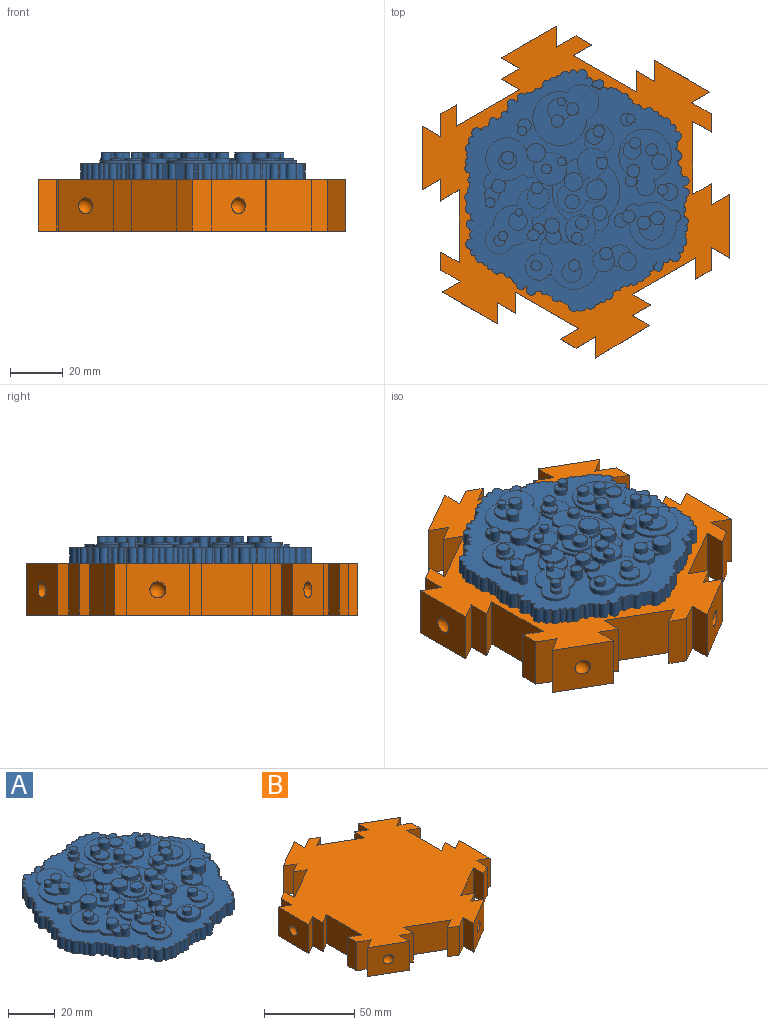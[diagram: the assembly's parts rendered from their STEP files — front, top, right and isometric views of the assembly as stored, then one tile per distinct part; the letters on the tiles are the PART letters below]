
ASSEMBLY  parts=2 mates=1
PART A: 301 faces, bbox 91.9x85.7x10 mm
  f0: cylinder r=4.09mm len=2.46mm, axis (0,0,-1), area 2.6mm2, adj f8,f185,f204,f299
  f1: cylinder r=4.09mm len=6.79mm, axis (0,0,-1), area 9.3mm2, adj f185,f204,f287,f299
  f2: cylinder r=2.88mm len=5.75mm, axis (0,0,-1), area 19.8mm2, adj f40,f41,f185,f191,f230,f297
  f3: cylinder r=2.79mm len=4.94mm, axis (0,0,-1), area 10.2mm2, adj f42,f185,f194,f227,f261,f295
  f4: cylinder r=2.79mm len=3.54mm, axis (0,0,-1), area 7.8mm2, adj f185,f227,f261,f295
  f5: cylinder r=2.49mm len=4.99mm, axis (0,0,-1), area 24.2mm2, adj f185,f225,f293
  f6: cylinder r=2.42mm len=4.85mm, axis (0,0,-1), area 23.1mm2, adj f185,f226,f291
  f7: cylinder r=3.19mm len=6.37mm, axis (0,0,-1), area 31.5mm2, adj f185,f229,f289
  f8: cylinder r=4.04mm len=8.09mm, axis (0,0,-1), area 30.1mm2, adj f0,f49,f50,f185,f191,f204,f216,f287
  f9: cylinder r=4.59mm len=8.54mm, axis (0,0,-1), area 16.5mm2, adj f203,f214,f283,f285
  f10: cylinder r=4.59mm len=1.25mm, axis (0,0,-1), area 1.7mm2, adj f203,f214,f283,f285
  f11: cylinder r=3.09mm len=4.48mm, axis (0,0,-1), area 6.8mm2, adj f185,f202,f203,f281
  f12: cylinder r=8.87mm len=16.72mm, axis (0,0,-1), area 30.2mm2, adj f185,f201,f203,f281
  f13: cylinder r=2.59mm len=5.18mm, axis (0,0,-1), area 24.3mm2, adj f185,f224,f281
  f14: cylinder r=2.17mm len=4.35mm, axis (0,0,-1), area 20.7mm2, adj f43,f44,f185,f200,f223,f279
  f15: cylinder r=3.37mm len=6.74mm, axis (0,0,-1), area 16.7mm2, adj f200,f211,f275
  f16: cylinder r=3.06mm len=6.12mm, axis (0,0,-1), area 14.5mm2, adj f198,f219,f273
  f17: cylinder r=4.33mm len=3.04mm, axis (0,0,-1), area 3.2mm2, adj f197,f210,f267,f271
  f18: cylinder r=4.33mm len=2.02mm, axis (0,0,-1), area 2.1mm2, adj f197,f210,f269,f271
  f19: cylinder r=4.33mm len=7.78mm, axis (0,0,-1), area 10.5mm2, adj f197,f210,f267,f269
  f20: cylinder r=6.22mm len=5.94mm, axis (0,0,-1), area 13.4mm2, adj f185,f220,f251,f265
  f21: cylinder r=6.22mm len=12.34mm, axis (0,0,-1), area 32.2mm2, adj f46,f47,f48,f185,f187,f194,f220,f251
  f22: cylinder r=5.63mm len=1mm, axis (0,0,-1), area 0.7mm2, adj f185,f193,f194,f265
  f23: cylinder r=3.37mm len=6.74mm, axis (0,0,-1), area 18.3mm2, adj f194,f209,f263
  f24: cylinder r=4.07mm len=1.49mm, axis (0,0,-1), area 1.9mm2, adj f185,f192,f194,f261
  f25: cylinder r=2.12mm len=4.24mm, axis (0,0,-1), area 9.7mm2, adj f190,f228,f259
  f26: cylinder r=7.51mm len=5.65mm, axis (0,0,-1), area 6.8mm2, adj f185,f189,f190,f257
  f27: cylinder r=7.51mm len=3.38mm, axis (0,0,-1), area 4.5mm2, adj f45,f185,f190,f257
  f28: cylinder r=2.07mm len=4.14mm, axis (0,0,-1), area 19.6mm2, adj f185,f222,f257
  f29: cylinder r=3.48mm len=6.96mm, axis (0,0,-1), area 19mm2, adj f190,f208,f255
  f30: cylinder r=5.52mm len=8.29mm, axis (0,0,-1), area 9.4mm2, adj f185,f188,f190,f253
  f31: cylinder r=4.2mm len=8.39mm, axis (0,0,-1), area 29.3mm2, adj f45,f185,f190,f221,f253
  f32: cylinder r=12.75mm len=15.85mm, axis (0,0,-1), area 22.2mm2, adj f52,f185,f187,f247
  f33: cylinder r=5.59mm len=5.4mm, axis (0,0,-1), area 5.7mm2, adj f38,f187,f207,f247
  f34: cylinder r=5.59mm len=11.17mm, axis (0,0,-1), area 31.8mm2, adj f35,f46,f51,f185,f187,f198,f207,f247
  f35: cylinder r=4.86mm len=3.39mm, axis (0,0,-1), area 3.6mm2, adj f34,f187,f207,f243
  f36: cylinder r=5.55mm len=11.1mm, axis (0,0,-1), area 22.6mm2, adj f37,f187,f207,f243
  f37: cylinder r=4.86mm len=7.02mm, axis (0,0,-1), area 10mm2, adj f36,f187,f207,f239
  f38: cylinder r=4.86mm len=5.68mm, axis (0,0,-1), area 6.3mm2, adj f33,f187,f207,f239
  f39: cylinder r=3.79mm len=7.58mm, axis (0,0,-1), area 19.3mm2, adj f191,f215,f237
  f40: cylinder r=4.86mm len=2.02mm, axis (0,0,-1), area 2.1mm2, adj f2,f53,f185,f191
  f41: cylinder r=4.86mm len=5.95mm, axis (0,0,-1), area 6.7mm2, adj f2,f185,f191,f217
  f42: cylinder r=4.07mm len=6.28mm, axis (0,0,-1), area 7.8mm2, adj f3,f185,f193,f194
  f43: cylinder r=9.91mm len=19.82mm, axis (0,0,-1), area 52.5mm2, adj f14,f185,f199,f200
  f44: cylinder r=9.91mm len=1mm, axis (0,0,-1), area 0.7mm2, adj f14,f185,f199,f200
  f45: cylinder r=5.52mm len=7.31mm, axis (0,0,-1), area 8.3mm2, adj f27,f31,f185,f190
  f46: cylinder r=12.75mm len=4.37mm, axis (0,0,-1), area 5.1mm2, adj f21,f34,f185,f187
  f47: cylinder r=12.75mm len=12.69mm, axis (0,0,-1), area 15.7mm2, adj f21,f185,f187,f205
  f48: cylinder r=5.63mm len=5.05mm, axis (0,0,-1), area 5.7mm2, adj f21,f185,f192,f194
  f49: cylinder r=9.09mm len=14.52mm, axis (0,0,-1), area 24mm2, adj f8,f185,f191,f217
  f50: cylinder r=9.09mm len=5.03mm, axis (0,0,-1), area 5.2mm2, adj f8,f185,f191,f205
  f51: cylinder r=5.59mm len=11.19mm, axis (0,0,-1), area 28.4mm2, adj f34,f185,f198
  f52: cylinder r=4.01mm len=6.9mm, axis (0,0,-1), area 8.4mm2, adj f32,f185,f187,f205
  f53: cylinder r=9.09mm len=1.93mm, axis (0,0,-1), area 2.5mm2, adj f40,f185,f191,f205
  f54: cylinder r=1.89mm len=6mm, axis (0,0,-1), area 28mm2, adj f55,f184,f185,f186
  f55: cylinder r=1.39mm len=6mm, axis (0,0,-1), area 14.6mm2, adj f54,f56,f185,f186
  f56: cylinder r=1.18mm len=6mm, axis (0,0,-1), area 19.7mm2, adj f55,f57,f185,f186
  f57: cylinder r=1.7mm len=6mm, axis (0,0,-1), area 27.3mm2, adj f56,f58,f185,f186
  f58: cylinder r=1.75mm len=6mm, axis (0,0,-1), area 10.8mm2, adj f57,f59,f185,f186
  f59: cylinder r=1.05mm len=6mm, axis (0,0,-1), area 17.7mm2, adj f58,f60,f185,f186
  f60: cylinder r=1.56mm len=6mm, axis (0,0,-1), area 10mm2, adj f59,f61,f185,f186
  f61: cylinder r=1.23mm len=6mm, axis (0,0,-1), area 16.4mm2, adj f60,f62,f185,f186
  f62: cylinder r=1.77mm len=6mm, axis (0,0,-1), area 33.5mm2, adj f61,f63,f185,f186
  f63: cylinder r=2.16mm len=6mm, axis (0,0,-1), area 5mm2, adj f62,f64,f185,f186
  f64: cylinder r=1.81mm len=6mm, axis (0,0,-1), area 40mm2, adj f63,f65,f185,f186
  f65: cylinder r=1.68mm len=6mm, axis (0,0,-1), area 13mm2, adj f64,f66,f185,f186
  f66: cylinder r=1.31mm len=6mm, axis (0,0,-1), area 23.8mm2, adj f65,f67,f185,f186
  f67: cylinder r=1.43mm len=6mm, axis (0,0,-1), area 14.6mm2, adj f66,f68,f185,f186
  f68: plane 6x0.07mm, normal (0.79,0.61,0), area 0.6mm2, adj f67,f69,f185,f186
  f69: cylinder r=1.62mm len=6mm, axis (0,0,-1), area 31mm2, adj f68,f70,f185,f186
  f70: cylinder r=1.2mm len=6mm, axis (0,0,-1), area 9.5mm2, adj f69,f71,f185,f186
  f71: plane 6x0.06mm, normal (0.79,0.61,0), area 0.4mm2, adj f70,f72,f185,f186
  f72: cylinder r=1.58mm len=6mm, axis (0,0,-1), area 20.4mm2, adj f71,f73,f185,f186
  f73: plane 6x0.03mm, normal (0.79,0.61,0), area 0.2mm2, adj f72,f74,f185,f186
  f74: cylinder r=1.97mm len=6mm, axis (0,0,-1), area 41.2mm2, adj f73,f75,f185,f186
  f75: plane 6x0.07mm, normal (0.79,0.61,0), area 0.5mm2, adj f74,f76,f185,f186
  f76: cylinder r=1.43mm len=6mm, axis (0,0,-1), area 24.2mm2, adj f75,f77,f185,f186
  f77: cylinder r=1.89mm len=6mm, axis (0,0,-1), area 28mm2, adj f76,f78,f185,f186
  f78: cylinder r=1.39mm len=6mm, axis (0,0,-1), area 14.6mm2, adj f77,f79,f185,f186
  f79: cylinder r=1.18mm len=6mm, axis (0,0,-1), area 19.7mm2, adj f78,f80,f185,f186
  f80: cylinder r=1.7mm len=6mm, axis (0,0,-1), area 27.3mm2, adj f79,f81,f185,f186
  f81: cylinder r=1.75mm len=6mm, axis (0,0,-1), area 10.8mm2, adj f80,f82,f185,f186
  f82: cylinder r=1.05mm len=6mm, axis (0,0,-1), area 17.7mm2, adj f81,f83,f185,f186
  f83: cylinder r=1.56mm len=6mm, axis (0,0,-1), area 10mm2, adj f82,f84,f185,f186
  f84: cylinder r=1.23mm len=6mm, axis (0,0,-1), area 16.4mm2, adj f83,f85,f185,f186
  f85: cylinder r=1.77mm len=6mm, axis (0,0,-1), area 24.5mm2, adj f84,f86,f185,f186
  f86: cylinder r=1.68mm len=6mm, axis (0,0,-1), area 12.4mm2, adj f85,f87,f185,f186
  f87: cylinder r=1.81mm len=6mm, axis (0,0,-1), area 13mm2, adj f86,f88,f185,f186
  f88: cylinder r=1.31mm len=6mm, axis (0,0,-1), area 14mm2, adj f87,f89,f185,f186
  f89: cylinder r=1.43mm len=6mm, axis (0,0,-1), area 23.1mm2, adj f88,f90,f185,f186
  f90: plane 6x4.18mm, normal (-0.14,0.99,0), area 25.3mm2, adj f89,f91,f185,f186
  f91: cylinder r=1.58mm len=6mm, axis (0,0,-1), area 5.1mm2, adj f90,f92,f185,f186
  f92: cylinder r=1.2mm len=6mm, axis (0,0,-1), area 14.2mm2, adj f91,f93,f185,f186
  f93: cylinder r=1.62mm len=6mm, axis (0,0,-1), area 46.1mm2, adj f92,f94,f185,f186
  f94: cylinder r=1.2mm len=6mm, axis (0,0,-1), area 10.2mm2, adj f93,f95,f185,f186
  f95: cylinder r=1.58mm len=6mm, axis (0,0,-1), area 22.1mm2, adj f94,f96,f185,f186
  f96: cylinder r=1.97mm len=6mm, axis (0,0,-1), area 42.8mm2, adj f95,f97,f185,f186
  f97: cylinder r=1.43mm len=6mm, axis (0,0,-1), area 25.3mm2, adj f96,f98,f185,f186
  f98: cylinder r=1.89mm len=6mm, axis (0,0,-1), area 28mm2, adj f97,f99,f185,f186
  f99: cylinder r=1.39mm len=6mm, axis (0,0,-1), area 14.6mm2, adj f98,f100,f185,f186
  f100: cylinder r=1.18mm len=6mm, axis (0,0,-1), area 19.7mm2, adj f99,f101,f185,f186
  f101: cylinder r=1.7mm len=6mm, axis (0,0,-1), area 27.3mm2, adj f100,f102,f185,f186
  f102: cylinder r=1.75mm len=6mm, axis (0,0,-1), area 10.8mm2, adj f101,f103,f185,f186
  f103: cylinder r=1.05mm len=6mm, axis (0,0,-1), area 17.7mm2, adj f102,f104,f185,f186
  f104: cylinder r=1.56mm len=6mm, axis (0,0,-1), area 10mm2, adj f103,f105,f185,f186
  f105: cylinder r=1.23mm len=6mm, axis (0,0,-1), area 16.4mm2, adj f104,f106,f185,f186
  f106: cylinder r=1.77mm len=6mm, axis (0,0,-1), area 33.5mm2, adj f105,f107,f185,f186
  f107: cylinder r=2.16mm len=6mm, axis (0,0,-1), area 5mm2, adj f106,f108,f185,f186
  f108: cylinder r=1.81mm len=6mm, axis (0,0,-1), area 40mm2, adj f107,f109,f185,f186
  f109: cylinder r=1.68mm len=6mm, axis (0,0,-1), area 13mm2, adj f108,f110,f185,f186
  f110: cylinder r=1.31mm len=6mm, axis (0,0,-1), area 23.8mm2, adj f109,f111,f185,f186
  f111: cylinder r=1.43mm len=6mm, axis (0,0,-1), area 14.1mm2, adj f110,f112,f185,f186
  f112: plane 6x0.11mm, normal (-0.93,0.38,0), area 0.7mm2, adj f111,f113,f185,f186
  f113: cylinder r=1.62mm len=6mm, axis (0,0,-1), area 30.6mm2, adj f112,f114,f185,f186
  f114: cylinder r=1.2mm len=6mm, axis (0,0,-1), area 9.2mm2, adj f113,f115,f185,f186
  f115: plane 6x0.1mm, normal (-0.93,0.38,0), area 0.6mm2, adj f114,f116,f185,f186
  f116: cylinder r=1.58mm len=6mm, axis (0,0,-1), area 20mm2, adj f115,f117,f185,f186
  f117: plane 6x0.04mm, normal (-0.93,0.38,0), area 0.2mm2, adj f116,f118,f185,f186
  f118: cylinder r=1.97mm len=6mm, axis (0,0,-1), area 41.1mm2, adj f117,f119,f185,f186
  f119: plane 6x0.07mm, normal (-0.93,0.38,0), area 0.5mm2, adj f118,f120,f185,f186
  f120: cylinder r=1.43mm len=6mm, axis (0,0,-1), area 23.7mm2, adj f119,f121,f185,f186
  f121: plane 6x0.05mm, normal (-0.79,-0.61,0), area 0.4mm2, adj f120,f122,f185,f186
  f122: cylinder r=1.89mm len=6mm, axis (0,0,-1), area 27.5mm2, adj f121,f123,f185,f186
  f123: cylinder r=1.39mm len=6mm, axis (0,0,-1), area 14.6mm2, adj f122,f124,f185,f186
  f124: cylinder r=1.18mm len=6mm, axis (0,0,-1), area 19.7mm2, adj f123,f125,f185,f186
  f125: cylinder r=1.7mm len=6mm, axis (0,0,-1), area 27.3mm2, adj f124,f126,f185,f186
  f126: cylinder r=1.75mm len=6mm, axis (0,0,-1), area 10.8mm2, adj f125,f127,f185,f186
  f127: cylinder r=1.05mm len=6mm, axis (0,0,-1), area 17.7mm2, adj f126,f128,f185,f186
  f128: cylinder r=1.56mm len=6mm, axis (0,0,-1), area 10mm2, adj f127,f129,f185,f186
  f129: cylinder r=1.23mm len=6mm, axis (0,0,-1), area 16.4mm2, adj f128,f130,f185,f186
  f130: cylinder r=1.77mm len=6mm, axis (0,0,-1), area 24.6mm2, adj f129,f131,f185,f186
  f131: cylinder r=1.68mm len=6mm, axis (0,0,-1), area 9.6mm2, adj f130,f132,f185,f186
  f132: cylinder r=1.81mm len=6mm, axis (0,0,-1), area 19.9mm2, adj f131,f133,f185,f186
  f133: cylinder r=1.31mm len=6mm, axis (0,0,-1), area 9.1mm2, adj f132,f134,f185,f186
  f134: cylinder r=1.43mm len=6mm, axis (0,0,-1), area 19mm2, adj f133,f135,f185,f186
  f135: plane 6x0.26mm, normal (-0.79,-0.61,0), area 2mm2, adj f134,f136,f185,f186
  f136: cylinder r=1.62mm len=6mm, axis (0,0,-1), area 36.1mm2, adj f135,f137,f185,f186
  f137: cylinder r=1.2mm len=6mm, axis (0,0,-1), area 10.2mm2, adj f136,f138,f185,f186
  f138: cylinder r=1.58mm len=6mm, axis (0,0,-1), area 22.1mm2, adj f137,f139,f185,f186
  f139: cylinder r=1.97mm len=6mm, axis (0,0,-1), area 42.8mm2, adj f138,f140,f185,f186
  f140: cylinder r=1.43mm len=6mm, axis (0,0,-1), area 23.7mm2, adj f139,f141,f185,f186
  f141: plane 6x0.48mm, normal (-0.79,-0.61,0), area 3.6mm2, adj f140,f142,f185,f186
  f142: plane 6x0.03mm, normal (0.14,-0.99,0), area 0.2mm2, adj f141,f143,f185,f186
  f143: cylinder r=1.89mm len=6mm, axis (0,0,-1), area 23.6mm2, adj f142,f144,f185,f186
  f144: cylinder r=1.39mm len=6mm, axis (0,0,-1), area 14.6mm2, adj f143,f145,f185,f186
  f145: cylinder r=1.18mm len=6mm, axis (0,0,-1), area 19.7mm2, adj f144,f146,f185,f186
  f146: cylinder r=1.7mm len=6mm, axis (0,0,-1), area 27.3mm2, adj f145,f147,f185,f186
  f147: cylinder r=1.75mm len=6mm, axis (0,0,-1), area 10.8mm2, adj f146,f148,f185,f186
  f148: cylinder r=1.05mm len=6mm, axis (0,0,-1), area 17.7mm2, adj f147,f149,f185,f186
  f149: cylinder r=1.56mm len=6mm, axis (0,0,-1), area 10mm2, adj f148,f150,f185,f186
  f150: cylinder r=1.23mm len=6mm, axis (0,0,-1), area 16.4mm2, adj f149,f151,f185,f186
  f151: cylinder r=1.77mm len=6mm, axis (0,0,-1), area 33.5mm2, adj f150,f152,f185,f186
  f152: cylinder r=2.16mm len=6mm, axis (0,0,-1), area 5mm2, adj f151,f153,f185,f186
  f153: cylinder r=1.81mm len=6mm, axis (0,0,-1), area 40mm2, adj f152,f154,f185,f186
  f154: cylinder r=1.68mm len=6mm, axis (0,0,-1), area 11.1mm2, adj f153,f155,f185,f186
  f155: plane 6x0.21mm, normal (0.14,-0.99,0), area 1.3mm2, adj f154,f156,f185,f186
  f156: cylinder r=1.31mm len=6mm, axis (0,0,-1), area 17.2mm2, adj f155,f157,f185,f186
  f157: plane 6x2.32mm, normal (0.14,-0.99,0), area 14mm2, adj f156,f158,f185,f186
  f158: cylinder r=1.62mm len=6mm, axis (0,0,-1), area 24.7mm2, adj f157,f159,f185,f186
  f159: plane 6x4mm, normal (0.14,-0.99,0), area 24.2mm2, adj f158,f160,f185,f186
  f160: cylinder r=1.97mm len=6mm, axis (0,0,-1), area 29.5mm2, adj f159,f161,f185,f186
  f161: plane 6x1.48mm, normal (0.14,-0.99,0), area 9mm2, adj f160,f162,f185,f186
  f162: plane 6x0.68mm, normal (0.93,-0.38,0), area 4.4mm2, adj f161,f163,f185,f186
  f163: cylinder r=1.43mm len=6mm, axis (0,0,-1), area 10mm2, adj f162,f164,f185,f186
  f164: plane 6x0.38mm, normal (0.93,-0.38,0), area 2.5mm2, adj f163,f165,f185,f186
  f165: cylinder r=1.89mm len=6mm, axis (0,0,-1), area 25.9mm2, adj f164,f166,f185,f186
  f166: cylinder r=1.39mm len=6mm, axis (0,0,-1), area 14.6mm2, adj f165,f167,f185,f186
  f167: cylinder r=1.18mm len=6mm, axis (0,0,-1), area 19.7mm2, adj f166,f168,f185,f186
  f168: cylinder r=1.7mm len=6mm, axis (0,0,-1), area 27.3mm2, adj f167,f169,f185,f186
  f169: cylinder r=1.75mm len=6mm, axis (0,0,-1), area 10.8mm2, adj f168,f170,f185,f186
  f170: cylinder r=1.05mm len=6mm, axis (0,0,-1), area 17.7mm2, adj f169,f171,f185,f186
  f171: cylinder r=1.56mm len=6mm, axis (0,0,-1), area 10mm2, adj f170,f172,f185,f186
  f172: cylinder r=1.23mm len=6mm, axis (0,0,-1), area 16.4mm2, adj f171,f173,f185,f186
  f173: cylinder r=1.77mm len=6mm, axis (0,0,-1), area 23.2mm2, adj f172,f174,f185,f186
  f174: cylinder r=1.68mm len=6mm, axis (0,0,-1), area 16.4mm2, adj f173,f175,f185,f186
  f175: cylinder r=1.81mm len=6mm, axis (0,0,-1), area 8mm2, adj f174,f176,f185,f186
  f176: cylinder r=1.31mm len=6mm, axis (0,0,-1), area 16.8mm2, adj f175,f177,f185,f186
  f177: cylinder r=1.43mm len=6mm, axis (0,0,-1), area 21.2mm2, adj f176,f178,f185,f186
  f178: plane 6x1.91mm, normal (0.93,-0.38,0), area 12.4mm2, adj f177,f179,f185,f186
  f179: cylinder r=1.2mm len=6mm, axis (0,0,-1), area 1.2mm2, adj f178,f180,f185,f186
  f180: cylinder r=1.62mm len=6mm, axis (0,0,-1), area 46.1mm2, adj f179,f181,f185,f186
  f181: cylinder r=1.2mm len=6mm, axis (0,0,-1), area 10.2mm2, adj f180,f182,f185,f186
  f182: cylinder r=1.58mm len=6mm, axis (0,0,-1), area 22.1mm2, adj f181,f183,f185,f186
  f183: cylinder r=1.97mm len=6mm, axis (0,0,-1), area 42.8mm2, adj f182,f184,f185,f186
  f184: cylinder r=1.43mm len=6mm, axis (0,0,-1), area 25.3mm2, adj f54,f183,f185,f186
  f185: plane 91.92x85.7mm, normal (0,0,1), area 2551.8mm2, adj f0,f1,f2,f3,f4,f5,f6,f7
  f186: plane 91.92x85.7mm, normal (0,0,-1), area 5729.6mm2, adj f54,f55,f56,f57,f58,f59,f60,f61
  f187: plane 26.07x25.46mm, normal (0,0,1), area 203.4mm2, adj f21,f32,f33,f34,f35,f36,f37,f38
  f188: cylinder r=7.51mm len=11.69mm, axis (0,0,-1), area 14mm2, adj f30,f185,f189,f190
  f189: cylinder r=5.41mm len=10.82mm, axis (0,0,-1), area 21mm2, adj f26,f185,f188,f190
  f190: plane 28.09x15mm, normal (0,0,1), area 209.9mm2, adj f25,f26,f27,f29,f30,f31,f45,f188
  f191: plane 23.98x18.17mm, normal (0,0,1), area 228mm2, adj f2,f8,f39,f40,f41,f49,f50,f53
  f192: cylinder r=8.03mm len=5.65mm, axis (0,0,-1), area 7.1mm2, adj f24,f48,f185,f194
  f193: cylinder r=8.03mm len=15.8mm, axis (0,0,-1), area 27.1mm2, adj f22,f42,f185,f194
  f194: plane 22.08x20.99mm, normal (0,0,1), area 207mm2, adj f3,f21,f22,f23,f24,f42,f48,f192
  f195: cylinder r=6.61mm len=13.21mm, axis (0,0,-1), area 25.1mm2, adj f185,f196,f197
  f196: cylinder r=10.22mm len=20.45mm, axis (0,0,-1), area 50.8mm2, adj f185,f195,f197
  f197: plane 26.54x20.45mm, normal (0,0,1), area 324mm2, adj f17,f18,f19,f195,f196,f267,f269,f271
  f198: plane 11.19x11mm, normal (0,0,1), area 54.1mm2, adj f16,f34,f51,f273
  f199: cylinder r=3.56mm len=7.13mm, axis (0,0,-1), area 16.1mm2, adj f43,f44,f185,f200
  f200: plane 22.92x20.52mm, normal (0,0,1), area 235.4mm2, adj f14,f15,f43,f44,f199,f212,f275,f277
  f201: cylinder r=2.32mm len=4.42mm, axis (0,0,-1), area 7.9mm2, adj f12,f185,f202,f203
  f202: cylinder r=8.87mm len=10.96mm, axis (0,0,-1), area 13.5mm2, adj f11,f185,f201,f203
  f203: plane 20.82x18.69mm, normal (0,0,1), area 178.5mm2, adj f9,f10,f11,f12,f201,f202,f281,f283
  f204: plane 8.18x6.79mm, normal (0,0,1), area 28.5mm2, adj f0,f1,f8,f287,f299
  f205: cylinder r=5.73mm len=11.47mm, axis (0,0,-1), area 51.6mm2, adj f47,f50,f52,f53,f185,f187,f191,f206
  f206: plane 11.47x11.47mm, normal (0,0,1), area 69.6mm2, adj f205,f233,f235
  f207: plane 26.46x16.7mm, normal (0,0,1), area 165.4mm2, adj f33,f34,f35,f36,f37,f38,f239,f241
  f208: plane 6.96x6.96mm, normal (0,0,1), area 34.7mm2, adj f29,f255
  f209: plane 6.74x6.74mm, normal (0,0,1), area 18.3mm2, adj f23,f263
  f210: plane 8.65x8.64mm, normal (0,0,1), area 39.6mm2, adj f17,f18,f19,f267,f269,f271
  f211: plane 6.74x6.4mm, normal (0,0,1), area 28.4mm2, adj f15,f275
  f212: cylinder r=2.98mm len=5.96mm, axis (0,0,-1), area 18.7mm2, adj f200,f213
  f213: plane 5.96x5.96mm, normal (0,0,1), area 27.9mm2, adj f212
  f214: plane 8.54x8.44mm, normal (0,0,1), area 41.7mm2, adj f9,f10,f283,f285
  f215: plane 7.58x7.4mm, normal (0,0,1), area 34.5mm2, adj f39,f237
  f216: plane 8.09x7.81mm, normal (0,0,1), area 38.2mm2, adj f8,f287
  f217: cylinder r=5.03mm len=10.06mm, axis (0,0,-1), area 53.6mm2, adj f41,f49,f185,f191,f218
  f218: plane 10.06x10.06mm, normal (0,0,1), area 67.4mm2, adj f217,f231
  f219: plane 6.12x5.57mm, normal (0,0,1), area 21.2mm2, adj f16,f273
  f220: plane 12.44x12.34mm, normal (0,0,1), area 97.9mm2, adj f20,f21,f249,f251,f265
  f221: plane 8.39x8.39mm, normal (0,0,1), area 45.5mm2, adj f31,f253
  f222: plane 4.14x3.67mm, normal (0,0,1), area 11.2mm2, adj f28,f257
  f223: plane 4.35x4.31mm, normal (0,0,1), area 13.8mm2, adj f14,f279
  f224: plane 5.18x5.05mm, normal (0,0,1), area 16.8mm2, adj f13,f281
  f225: plane 4.99x4.69mm, normal (0,0,1), area 14.9mm2, adj f5,f293
  f226: plane 4.85x4.85mm, normal (0,0,1), area 11.7mm2, adj f6,f291
  f227: plane 5.57x4.94mm, normal (0,0,1), area 17.6mm2, adj f3,f4,f261,f295
  f228: plane 4.24x3.59mm, normal (0,0,1), area 10.3mm2, adj f25,f259
  f229: plane 6.37x6.17mm, normal (0,0,1), area 24.6mm2, adj f7,f289
  f230: plane 5.75x5.75mm, normal (0,0,1), area 21.7mm2, adj f2,f297
  f231: cylinder r=1.96mm len=3.93mm, axis (0,0,-1), area 24.7mm2, adj f218,f232
  f232: plane 3.93x3.93mm, normal (0,0,1), area 12.1mm2, adj f231
  f233: cylinder r=2.46mm len=4.93mm, axis (0,0,-1), area 31mm2, adj f206,f234
  f234: plane 4.93x4.93mm, normal (0,0,1), area 19.1mm2, adj f233
  f235: cylinder r=2.16mm len=4.32mm, axis (0,0,-1), area 27.1mm2, adj f206,f236
  f236: plane 4.32x4.32mm, normal (0,0,1), area 14.7mm2, adj f235
  f237: cylinder r=2.15mm len=4.31mm, axis (0,0,-1), area 33.2mm2, adj f39,f191,f215,f238
  f238: plane 4.31x4.31mm, normal (0,0,1), area 14.6mm2, adj f237
  f239: cylinder r=3.82mm len=7.64mm, axis (0,0,-1), area 49.1mm2, adj f37,f38,f187,f207,f240
  f240: plane 7.64x7.64mm, normal (0,0,1), area 45.8mm2, adj f239
  f241: cylinder r=2.74mm len=5.47mm, axis (0,0,-1), area 34.4mm2, adj f207,f242
  f242: plane 5.47x5.47mm, normal (0,0,1), area 23.5mm2, adj f241
  f243: cylinder r=3.49mm len=6.97mm, axis (0,0,-1), area 56.5mm2, adj f35,f36,f187,f207,f244
  f244: plane 6.97x6.97mm, normal (0,0,1), area 38.2mm2, adj f243
  f245: cylinder r=2.77mm len=5.54mm, axis (0,0,-1), area 52.3mm2, adj f187,f246
  f246: plane 5.54x5.54mm, normal (0,0,1), area 24.1mm2, adj f245
  f247: cylinder r=2.25mm len=4.5mm, axis (0,0,-1), area 33.7mm2, adj f32,f33,f34,f185,f187,f207,f248
  f248: plane 4.5x4.5mm, normal (0,0,1), area 15.9mm2, adj f247
  f249: cylinder r=1.84mm len=3.68mm, axis (0,0,-1), area 23.1mm2, adj f220,f250
  f250: plane 3.68x3.68mm, normal (0,0,1), area 10.6mm2, adj f249
  f251: cylinder r=1.66mm len=4mm, axis (0,0,-1), area 27.3mm2, adj f20,f21,f185,f220,f252
  f252: plane 3.32x3.32mm, normal (0,0,1), area 8.6mm2, adj f251
  f253: cylinder r=2.25mm len=4.51mm, axis (0,0,-1), area 42.6mm2, adj f30,f31,f185,f190,f221,f254
  f254: plane 4.51x4.51mm, normal (0,0,1), area 16mm2, adj f253
  f255: cylinder r=1.42mm len=3mm, axis (0,0,-1), area 22.6mm2, adj f29,f190,f208,f256
  f256: plane 2.84x2.84mm, normal (0,0,1), area 6.4mm2, adj f255
  f257: cylinder r=2.16mm len=4.32mm, axis (0,0,-1), area 43.7mm2, adj f26,f27,f28,f185,f190,f222,f258
  f258: plane 4.32x4.32mm, normal (0,0,1), area 14.7mm2, adj f257
  f259: cylinder r=1.81mm len=3.62mm, axis (0,0,-1), area 30.2mm2, adj f25,f190,f228,f260
  f260: plane 3.62x3.62mm, normal (0,0,1), area 10.3mm2, adj f259
  f261: cylinder r=2.57mm len=5.13mm, axis (0,0,-1), area 48.7mm2, adj f3,f4,f24,f185,f194,f227,f262
  f262: plane 5.13x5.13mm, normal (0,0,1), area 20.7mm2, adj f261
  f263: cylinder r=2.37mm len=4.73mm, axis (0,0,-1), area 32.7mm2, adj f23,f194,f209,f264
  f264: plane 4.73x4.73mm, normal (0,0,1), area 17.6mm2, adj f263
  f265: cylinder r=3.49mm len=6.97mm, axis (0,0,-1), area 69.6mm2, adj f20,f21,f22,f185,f194,f220,f266
  f266: plane 6.97x6.97mm, normal (0,0,1), area 38.2mm2, adj f265
  f267: cylinder r=2.34mm len=4.67mm, axis (0,0,-1), area 38mm2, adj f17,f19,f197,f210,f268
  f268: plane 4.67x4.67mm, normal (0,0,1), area 17.1mm2, adj f267
  f269: cylinder r=1.61mm len=3.22mm, axis (0,0,-1), area 23.2mm2, adj f18,f19,f197,f210,f270
  f270: plane 3.22x3.22mm, normal (0,0,1), area 8.1mm2, adj f269
  f271: cylinder r=2.36mm len=4.73mm, axis (0,0,-1), area 39.8mm2, adj f17,f18,f197,f210,f272
  f272: plane 4.73x4.73mm, normal (0,0,1), area 17.6mm2, adj f271
  f273: cylinder r=2.16mm len=4.33mm, axis (0,0,-1), area 34.8mm2, adj f16,f198,f219,f274
  f274: plane 4.33x4.33mm, normal (0,0,1), area 14.7mm2, adj f273
  f275: cylinder r=2.12mm len=4.24mm, axis (0,0,-1), area 34.1mm2, adj f15,f200,f211,f276
  f276: plane 4.24x4.24mm, normal (0,0,1), area 14.1mm2, adj f275
  f277: cylinder r=2.29mm len=4.59mm, axis (0,0,-1), area 43.2mm2, adj f200,f278
  f278: plane 4.59x4.59mm, normal (0,0,1), area 16.5mm2, adj f277
  f279: cylinder r=2.4mm len=4.8mm, axis (0,0,-1), area 42.8mm2, adj f14,f200,f223,f280
  f280: plane 4.8x4.8mm, normal (0,0,1), area 18.1mm2, adj f279
  f281: cylinder r=2.38mm len=4.77mm, axis (0,0,-1), area 42.9mm2, adj f11,f12,f13,f185,f203,f224,f282
  f282: plane 4.77x4.77mm, normal (0,0,1), area 17.9mm2, adj f281
  f283: cylinder r=2.52mm len=5.04mm, axis (0,0,-1), area 38.8mm2, adj f9,f10,f203,f214,f284
  f284: plane 5.04x5.04mm, normal (0,0,1), area 19.9mm2, adj f283
  f285: cylinder r=2.56mm len=5.12mm, axis (0,0,-1), area 41.3mm2, adj f9,f10,f203,f214,f286
  f286: plane 5.12x5.12mm, normal (0,0,1), area 20.6mm2, adj f285
  f287: cylinder r=2.43mm len=4.86mm, axis (0,0,-1), area 42.5mm2, adj f1,f8,f185,f204,f216,f288
  f288: plane 4.86x4.86mm, normal (0,0,1), area 18.5mm2, adj f287
  f289: cylinder r=2mm len=4mm, axis (0,0,-1), area 38.6mm2, adj f7,f185,f229,f290
  f290: plane 3.99x3.99mm, normal (0,0,1), area 12.5mm2, adj f289
  f291: cylinder r=1.69mm len=4mm, axis (0,0,-1), area 30.8mm2, adj f6,f185,f226,f292
  f292: plane 3.37x3.37mm, normal (0,0,1), area 8.9mm2, adj f291
  f293: cylinder r=1.68mm len=4mm, axis (0,0,-1), area 33.1mm2, adj f5,f185,f225,f294
  f294: plane 3.36x3.36mm, normal (0,0,1), area 8.8mm2, adj f293
  f295: cylinder r=1.86mm len=4mm, axis (0,0,-1), area 38.8mm2, adj f3,f4,f185,f227,f296
  f296: plane 3.73x3.73mm, normal (0,0,1), area 10.9mm2, adj f295
  f297: cylinder r=2.84mm len=5.68mm, axis (0,0,-1), area 62.7mm2, adj f2,f185,f230,f298
  f298: plane 5.68x5.68mm, normal (0,0,1), area 25.4mm2, adj f297
  f299: cylinder r=3.36mm len=6.71mm, axis (0,0,-1), area 76mm2, adj f0,f1,f185,f204,f300
  f300: plane 6.71x6.71mm, normal (0,0,1), area 35.4mm2, adj f299
PART B: 68 faces, bbox 116x125.4x19.5 mm
  f0: plane 19.5x6.91mm, normal (-0.5,0.87,0), area 155.6mm2, adj f1,f53,f54,f55
  f1: plane 19.5x7.98mm, normal (1,0,0), area 155.6mm2, adj f0,f2,f54,f55
  f2: plane 19.5x6.91mm, normal (-0.5,0.87,0), area 155.6mm2, adj f1,f3,f54,f55
  f3: plane 27.51x19.5mm, normal (1,0,0), area 536.5mm2, adj f2,f4,f54,f55
  f4: plane 19.5x6.91mm, normal (-0.5,-0.87,0), area 155.6mm2, adj f3,f5,f54,f55
  f5: plane 19.5x6.83mm, normal (1,0,0), area 133.1mm2, adj f4,f6,f54,f55
  f6: plane 19.5x7.41mm, normal (0.5,0.87,0), area 166.9mm2, adj f5,f7,f54,f55
  f7: plane 19.5x6.91mm, normal (0.5,-0.87,0), area 155.6mm2, adj f6,f8,f54,f55
  f8: plane 20.83x19.5mm, normal (0.5,0.87,0), area 440.2mm2, adj f7,f9,f54,f55,f67
  f9: plane 19.5x7.98mm, normal (-1,0,0), area 155.6mm2, adj f8,f10,f54,f55
  f10: plane 19.5x6.91mm, normal (0.5,0.87,0), area 155.6mm2, adj f9,f11,f54,f55
  f11: plane 19.5x7.98mm, normal (-1,0,0), area 155.6mm2, adj f10,f12,f54,f55
  f12: plane 23.83x19.5mm, normal (0.5,0.87,0), area 536.5mm2, adj f11,f13,f54,f55
  f13: plane 19.5x6.91mm, normal (0.5,-0.87,0), area 155.6mm2, adj f12,f14,f54,f55
  f14: plane 19.5x5.91mm, normal (0.5,0.87,0), area 133.1mm2, adj f13,f15,f54,f55
  f15: plane 19.5x7.35mm, normal (-0.5,0.87,0), area 165.5mm2, adj f14,f16,f54,f55
  f16: plane 19.5x7.98mm, normal (1,0,0), area 155.6mm2, adj f15,f17,f54,f55
  f17: plane 20.88x19.5mm, normal (-0.5,0.87,0), area 441.2mm2, adj f16,f18,f54,f55,f65
  f18: plane 19.5x6.91mm, normal (-0.5,-0.87,0), area 155.6mm2, adj f17,f19,f54,f55
  f19: plane 19.5x6.93mm, normal (-0.5,0.87,0), area 156mm2, adj f18,f20,f54,f55
  f20: plane 19.5x6.92mm, normal (-0.5,-0.87,0), area 155.7mm2, adj f19,f21,f54,f55
  f21: plane 23.84x19.5mm, normal (-0.5,0.87,0), area 536.7mm2, adj f20,f22,f54,f55
  f22: plane 19.5x7.98mm, normal (1,0,0), area 155.6mm2, adj f21,f23,f54,f55
  f23: plane 19.5x5.91mm, normal (-0.5,0.87,0), area 133.1mm2, adj f22,f24,f54,f55
  f24: plane 19.5x8.56mm, normal (-1,0,0), area 166.8mm2, adj f23,f25,f54,f55
  f25: plane 19.5x6.92mm, normal (0.5,0.87,0), area 155.7mm2, adj f24,f26,f54,f55
  f26: plane 24.05x19.5mm, normal (-1,0,0), area 440.2mm2, adj f25,f27,f54,f55,f63
  f27: plane 19.5x6.91mm, normal (0.5,-0.87,0), area 155.6mm2, adj f26,f28,f54,f55
  f28: plane 19.5x8.28mm, normal (-1,0,0), area 161.4mm2, adj f27,f29,f54,f55
  f29: plane 19.5x6.91mm, normal (0.53,-0.85,0), area 158.9mm2, adj f28,f30,f54,f55
  f30: plane 27.55x19.5mm, normal (-1,0,0), area 537.2mm2, adj f29,f31,f54,f55
  f31: plane 19.5x6.91mm, normal (0.5,0.87,0), area 155.6mm2, adj f30,f32,f54,f55
  f32: plane 19.5x6.83mm, normal (-1,0,0), area 133.1mm2, adj f31,f33,f54,f55
  f33: plane 19.5x7.41mm, normal (-0.5,-0.87,0), area 166.9mm2, adj f32,f34,f54,f55
  f34: plane 19.5x6.91mm, normal (-0.5,0.87,0), area 155.6mm2, adj f33,f35,f54,f55
  f35: plane 20.83x19.5mm, normal (-0.5,-0.87,0), area 440.2mm2, adj f34,f36,f54,f55,f61
  f36: plane 19.5x7.98mm, normal (1,0,0), area 155.6mm2, adj f35,f37,f54,f55
  f37: plane 19.5x6.91mm, normal (-0.5,-0.87,0), area 155.6mm2, adj f36,f38,f54,f55
  f38: plane 19.5x7.98mm, normal (1,0,0), area 155.6mm2, adj f37,f39,f54,f55
  f39: plane 23.83x19.5mm, normal (-0.5,-0.87,0), area 536.5mm2, adj f38,f40,f54,f55
  f40: plane 19.5x6.91mm, normal (-0.5,0.87,0), area 155.6mm2, adj f39,f41,f54,f55
  f41: plane 19.5x5.91mm, normal (-0.5,-0.87,0), area 133.1mm2, adj f40,f42,f54,f55
  f42: plane 19.5x7.41mm, normal (0.5,-0.87,0), area 166.9mm2, adj f41,f43,f54,f55
  f43: plane 19.5x7.96mm, normal (-1,0,0), area 155.3mm2, adj f42,f44,f54,f55
  f44: plane 20.36x19.5mm, normal (0.52,-0.86,0), area 434.8mm2, adj f43,f45,f54,f55,f57
  f45: plane 19.5x6.44mm, normal (0.5,0.87,0), area 145.1mm2, adj f44,f46,f54,f55
  f46: plane 19.5x6.91mm, normal (0.5,-0.87,0), area 155.6mm2, adj f45,f47,f54,f55
  f47: plane 19.5x6.91mm, normal (0.5,0.87,0), area 155.6mm2, adj f46,f48,f54,f55
  f48: plane 23.83x19.5mm, normal (0.5,-0.87,0), area 536.5mm2, adj f47,f49,f54,f55
  f49: plane 19.5x7.98mm, normal (-1,0,0), area 155.6mm2, adj f48,f50,f54,f55
  f50: plane 19.5x5.91mm, normal (0.5,-0.87,0), area 133.1mm2, adj f49,f51,f54,f55
  f51: plane 19.5x8.56mm, normal (1,0,0), area 166.9mm2, adj f50,f52,f54,f55
  f52: plane 19.5x6.91mm, normal (-0.5,-0.87,0), area 155.6mm2, adj f51,f53,f54,f55
  f53: plane 24.05x19.5mm, normal (1,0,0), area 440.2mm2, adj f0,f52,f54,f55,f59
  f54: plane 125.36x115.97mm, normal (0,0,1), area 8886.2mm2, adj f0,f1,f2,f3,f4,f5,f6,f7
  f55: plane 125.36x115.97mm, normal (0,0,-1), area 8886.2mm2, adj f0,f1,f2,f3,f4,f5,f6,f7
  f56: sphere r=3.03mm, area 57.6mm2, adj f57
  f57: cylinder r=3.03mm len=6.05mm, axis (-0.52,0.86,0), area 0.2mm2, adj f44,f56
  f58: sphere r=3.03mm, area 57.6mm2, adj f59
  f59: cylinder r=3.03mm len=6.05mm, axis (-1,0,0), area 0.2mm2, adj f53,f58
  f60: sphere r=3.03mm, area 57.6mm2, adj f61
  f61: cylinder r=3.03mm len=6.05mm, axis (0.5,0.87,0), area 0.2mm2, adj f35,f60
  f62: sphere r=3.03mm, area 57.6mm2, adj f63
  f63: cylinder r=3.03mm len=6.05mm, axis (1,0,0), area 0.2mm2, adj f26,f62
  f64: sphere r=3.03mm, area 57.6mm2, adj f65
  f65: cylinder r=3.03mm len=6.05mm, axis (0.5,-0.87,0), area 0.2mm2, adj f17,f64
  f66: sphere r=3.03mm, area 57.6mm2, adj f67
  f67: cylinder r=3.03mm len=6.05mm, axis (-0.5,-0.87,0), area 0.2mm2, adj f8,f66
PLACE A rot(axis=(0,0,-1),35deg) t=(-0.33,-0.67,9.64)mm
PLACE B t=(-0.03,-0.29,-10.36)mm
MATE revolute A.f186 <-> B.f54  axis (0,0,-1) through (-0.04,-0.25,9.64)mm
